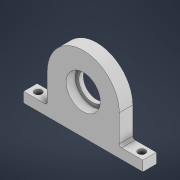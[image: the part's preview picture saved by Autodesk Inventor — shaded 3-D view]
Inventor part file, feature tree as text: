
AUTODESK INVENTOR PART (.ipt)
format: ipt  version: 2021 (Build 250183000, 183)  size: 309,248 bytes
history: native  units: mm
features: extrude x6, sketch x6, fillet x2, other x1
ambient origin geometry x8: Origin, YZ Plane, XZ Plane, XY Plane, X Axis, Y Axis, Z Axis, Center Point
bodies: Volumenkörper1 (feature_tree)
feature tree (15):
  other  "Halterung_Differential_Mitte"
  extrude  "Extrusion1"  Depth=32.0mm
  extrude  "Extrusion2"  Depth=10.5mm
  fillet  "Rundung1"  Radius=3.0mm
  fillet  "Rundung2"  Radius=6.0mm
  extrude  "Extrusion3"  Depth=1.0mm
  extrude  "Extrusion4"  Depth=4.0mm TaperAngle=0.0deg
  extrude  "Extrusion5"  Depth=5.0mm TaperAngle=0.0deg
  extrude  "Extrusion6"  Depth=3.0mm
  sketch  "Skizze1"  dims[d0=32.0mm d1=32.0mm]
  sketch  "Skizze2"  dims[d4=6.0mm d5=0.0mm d6=10.5mm d7=3.0mm d8=6.0mm d9=0.0mm]
  sketch  "Skizze3"  dims[d10=16.0mm d11=1.0mm]
  sketch  "Skizze4"  dims[d12=15.2mm d13=4.0mm d14=0.0mm]
  sketch  "Skizze5"  dims[d15=12.0mm d16=5.0mm d17=0.0mm]
  sketch  "Skizze6"  dims[d18=3.2mm d19=3.2mm d20=3.0mm d21=3.5mm d22=3.5mm d23=3.0mm d24=5.0mm d25=0.0mm d26=3.2mm d27=3.2mm d28=1.5mm d29=0.0mm]
